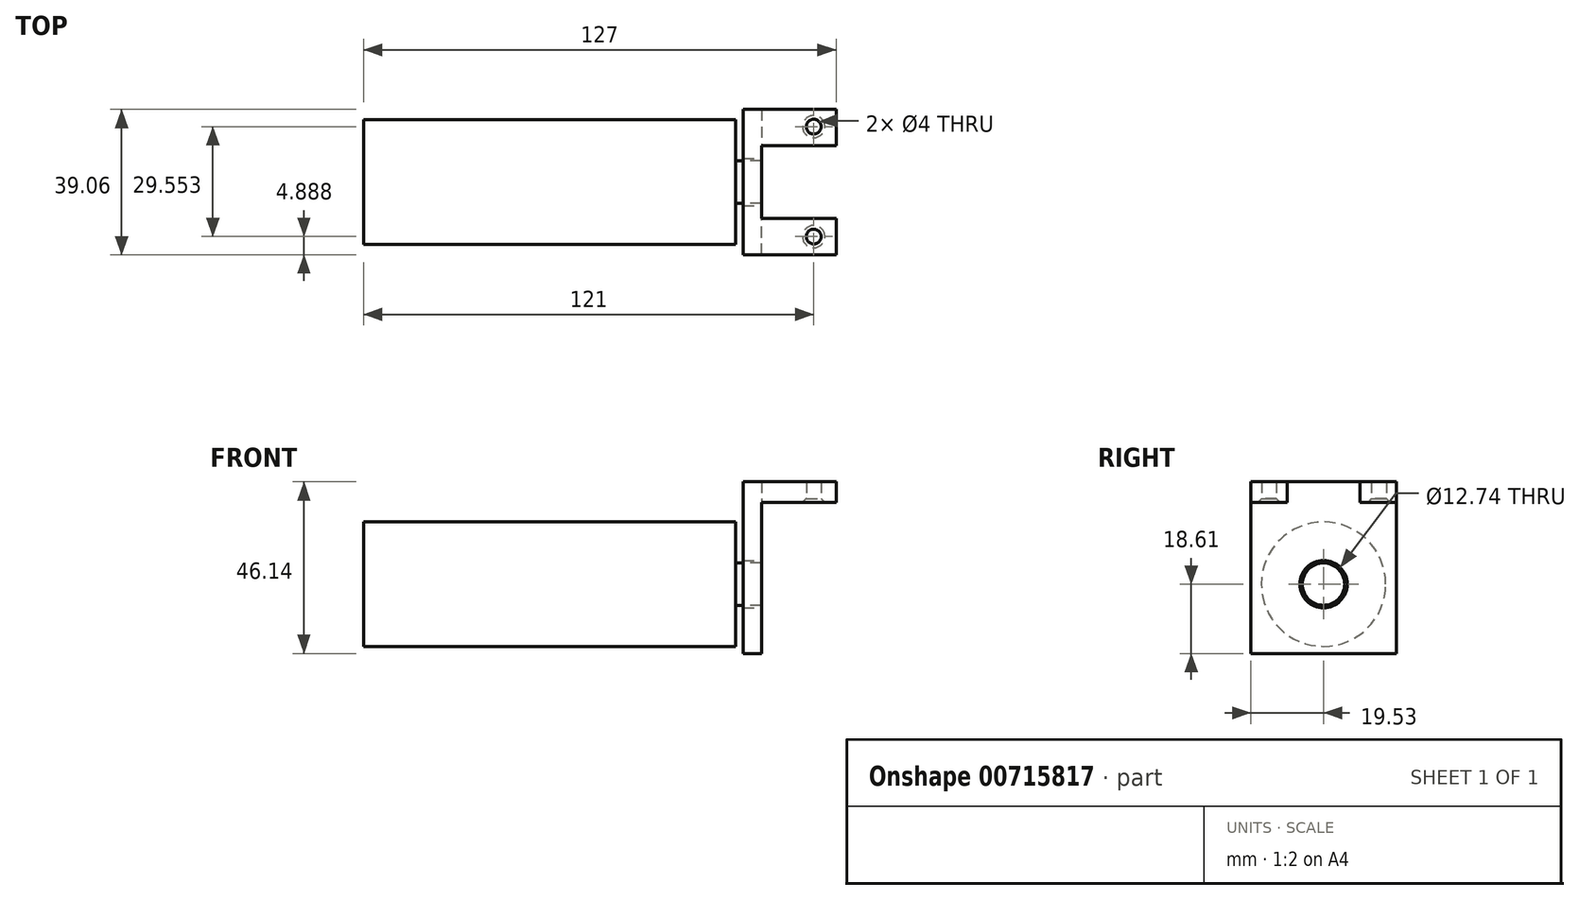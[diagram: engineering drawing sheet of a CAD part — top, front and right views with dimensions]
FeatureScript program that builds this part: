
annotation { "Feature Type Name" : "Feature", "Feature Type Description" : "" }
export const myFeature = defineFeature(function(context is Context, id is Id, definition is map)
    precondition{}
    {
        {
            var Q0;
            Q0=qCreatedBy(makeId("Right.planeOp"),FACE);
            var sketch = newSketch(context, id + "F0", { "sketchPlane" : qUnion([Q0])});
            skCircle(sketch, "E0", {"center": v(0, 0) * mm, "radius": 16.72 * mm});
            skSolve(sketch);
        }
        {
            var Q0;
            Q0 = qSketchRegion(id + "F0", true);
            extrude(context, id + "F1", {"entities" : qUnion([Q0]), "depth" : 100 * mm, "offsetDistance" : 25 * mm});
        }
        {
            var Q0;
            Q0=makeQuery(id+"F1.opExtrude","CAP_FACE",FACE,{"disambiguationData":[OSD([sQuery(id+"F0.wireOp",EDGE,"E0")])],"isStart":false});
            var sketch = newSketch(context, id + "F2", { "sketchPlane" : qUnion([Q0])});
            skCircle(sketch, "E1", {"center": v(0, 0) * mm, "radius": 5.68 * mm});
            skSolve(sketch);
        }
        {
            var Q0;
            Q0=makeQuery(id+"F2.imprint","IMPRINT",FACE,{"disambiguationData":[TD([[makeQuery(id+"F2.imprint","IMPRINT",EDGE,{"derivedFrom":sQuery(id+"F2.wireOp",EDGE,"E1")}),1.0]])]});
            extrude(context, id + "F3", {"entities" : qUnion([Q0]), "operationType" : NewBodyOperationType.ADD, "depth" : 7 * mm, "offsetDistance" : 25 * mm});
        }
        {
            var Q0;
            Q0=makeQuery(id+"F3.opExtrude","CAP_FACE",FACE,{"disambiguationData":[OSD([sQuery(id+"F2.wireOp",EDGE,"E1")])],"isStart":false});
            var sketch = newSketch(context, id + "F4", { "sketchPlane" : qUnion([Q0])});
            skLineSegment(sketch, "E2.bottom", {"start": v(-19.53, 27.53) * mm, "end": v(19.53, 27.53) * mm});
            skLineSegment(sketch, "E2.top", {"start": v(-19.53, -18.61) * mm, "end": v(19.53, -18.61) * mm});
            skLineSegment(sketch, "E2.left", {"start": v(-19.53, 27.53) * mm, "end": v(-19.53, -18.61) * mm});
            skLineSegment(sketch, "E2.right", {"start": v(19.53, 27.53) * mm, "end": v(19.53, -18.61) * mm});
            skCircle(sketch, "E3", {"center": v(0, 0) * mm, "radius": 6.37 * mm});
            skSolve(sketch);
        }
        {
            var Q0;
            Q0 = qSketchRegion(id + "F4", true);
            extrude(context, id + "F5", {"entities" : qUnion([Q0]), "depth" : -5 * mm, "offsetDistance" : 25 * mm});
        }
        {
            var Q0;
            Q0=makeQuery(id+"F5.opExtrude","CAP_FACE",FACE,{"disambiguationData":[OSD([sQuery(id+"F4.wireOp",EDGE,"E2.bottom"),sQuery(id+"F4.wireOp",EDGE,"E2.top"),sQuery(id+"F4.wireOp",EDGE,"E2.left"),sQuery(id+"F4.wireOp",EDGE,"E2.right"),sQuery(id+"F4.wireOp",EDGE,"E3")])],"isStart":true});
            var sketch = newSketch(context, id + "F6", { "sketchPlane" : qUnion([Q0])});
            skLineSegment(sketch, "E4.bottom", {"start": v(-19.53, 27.53) * mm, "end": v(-9.75, 27.53) * mm});
            skLineSegment(sketch, "E4.top", {"start": v(-19.53, 22.03) * mm, "end": v(-9.75, 22.03) * mm});
            skLineSegment(sketch, "E4.left", {"start": v(-19.53, 27.53) * mm, "end": v(-19.53, 22.03) * mm});
            skLineSegment(sketch, "E4.right", {"start": v(-9.75, 27.53) * mm, "end": v(-9.75, 22.03) * mm});
            skLineSegment(sketch, "E5.bottom", {"start": v(19.53, 27.53) * mm, "end": v(9.75, 27.53) * mm});
            skLineSegment(sketch, "E5.top", {"start": v(19.53, 22.03) * mm, "end": v(9.75, 22.03) * mm});
            skLineSegment(sketch, "E5.left", {"start": v(19.53, 27.53) * mm, "end": v(19.53, 22.03) * mm});
            skLineSegment(sketch, "E5.right", {"start": v(9.75, 27.53) * mm, "end": v(9.75, 22.03) * mm});
            skSolve(sketch);
        }
        {
            var Q0;
            Q0 = qSketchRegion(id + "F6", true);
            extrude(context, id + "F7", {"entities" : qUnion([Q0]), "operationType" : NewBodyOperationType.ADD, "depth" : 20 * mm, "offsetDistance" : 25 * mm});
        }
        {
            var Q0;
            Q0=makeQuery(id+"F7.opExtrude","SWEPT_FACE",FACE,{"disambiguationData":[OSD([sQuery(id+"F6.wireOp",EDGE,"E4.top")])]});
            var sketch = newSketch(context, id + "F8", { "sketchPlane" : qUnion([Q0])});
            skPoint(sketch, "E6", {"position": v(121, 14.64) * mm});
            skPoint(sketch, "E7", {"position": v(121, -14.91) * mm});
            skSolve(sketch);
        }
        {
            var Q0;
            Q0=sQuery(id+"F8.wireOp",VERTEX,"E6");
            var Q1;
            Q1=makeQuery(id+"F5.opExtrude","SWEPT_BODY",BODY,{"disambiguationData":[OSD([sQuery(id+"F4.wireOp",EDGE,"E2.bottom"),sQuery(id+"F4.wireOp",EDGE,"E2.top"),sQuery(id+"F4.wireOp",EDGE,"E2.left"),sQuery(id+"F4.wireOp",EDGE,"E2.right"),sQuery(id+"F4.wireOp",EDGE,"E3")])]});
            hole(context, id + "F9", {"style" : HoleStyle.C_SINK, "endStyle" : HoleEndStyle.THROUGH, "holeDiameter" : 4 * mm, "cSinkDiameter" : 6 * mm, "cSinkAngle" : 90 * degree, "majorDiameter" : 5 * mm, "isTappedThrough" : true, "tappedDepth" : 12 * mm, "tapClearance" : 3, "locations" : qUnion([Q0]), "scope" : qUnion([Q1])});
        }
        {
            var Q0;
            Q0=sQuery(id+"F8.wireOp",VERTEX,"E7");
            var Q1;
            Q1=makeQuery(id+"F5.opExtrude","SWEPT_BODY",BODY,{"disambiguationData":[OSD([sQuery(id+"F4.wireOp",EDGE,"E2.bottom"),sQuery(id+"F4.wireOp",EDGE,"E2.top"),sQuery(id+"F4.wireOp",EDGE,"E2.left"),sQuery(id+"F4.wireOp",EDGE,"E2.right"),sQuery(id+"F4.wireOp",EDGE,"E3")])]});
            hole(context, id + "F10", {"style" : HoleStyle.C_SINK, "endStyle" : HoleEndStyle.THROUGH, "holeDiameter" : 4 * mm, "cSinkDiameter" : 6 * mm, "cSinkAngle" : 90 * degree, "majorDiameter" : 5 * mm, "isTappedThrough" : true, "tappedDepth" : 12 * mm, "tapClearance" : 3, "locations" : qUnion([Q0]), "scope" : qUnion([Q1])});
        }
    });
